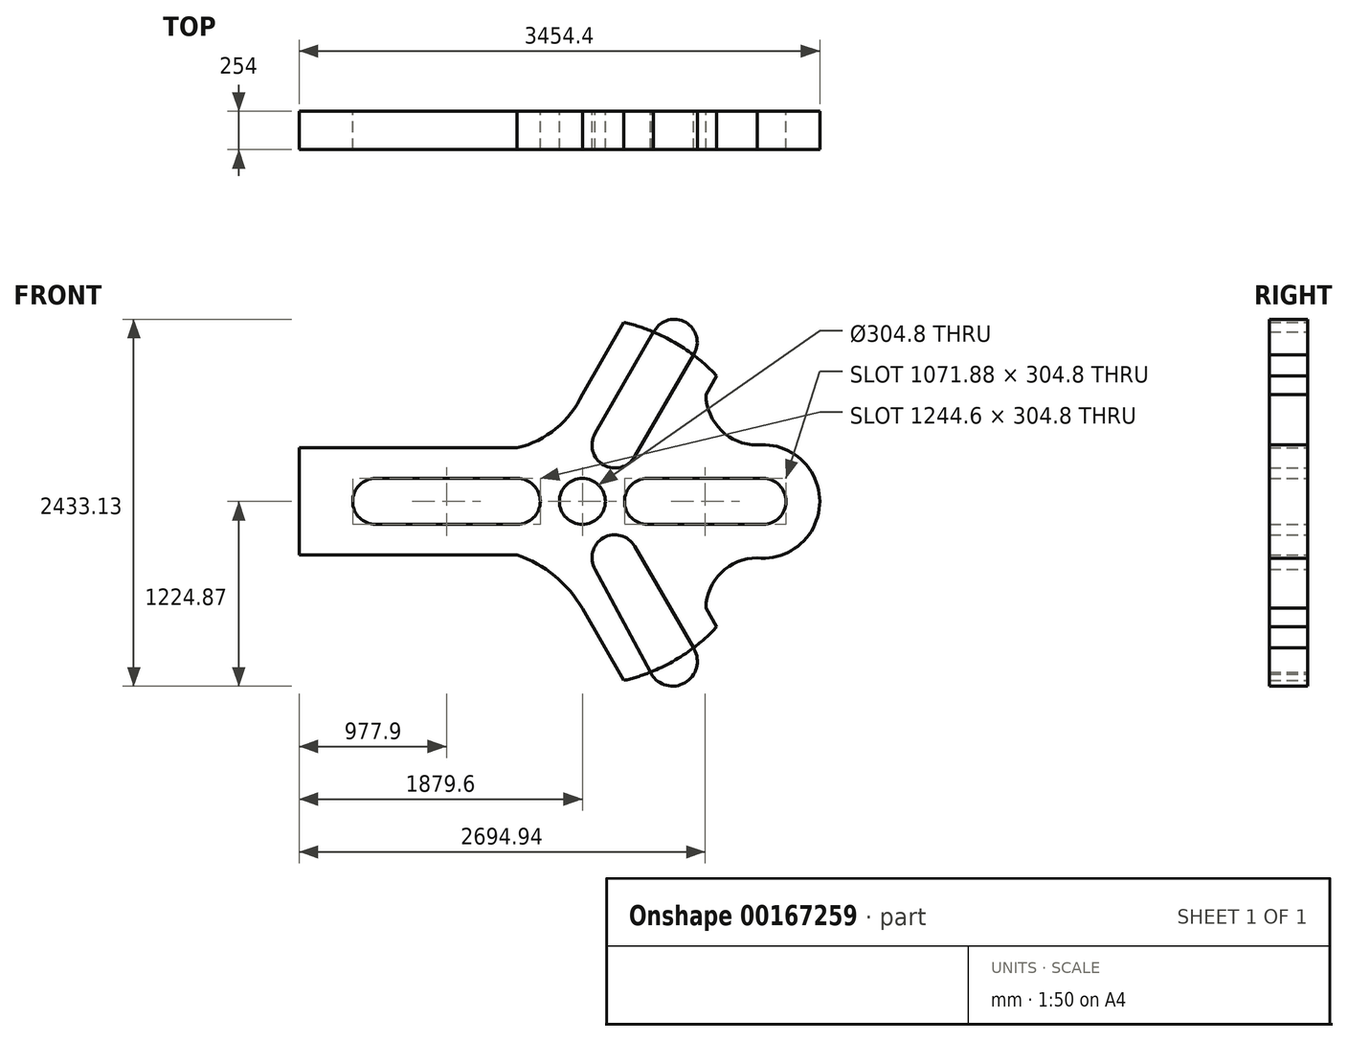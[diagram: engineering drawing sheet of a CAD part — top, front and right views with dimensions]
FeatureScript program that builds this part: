
annotation { "Feature Type Name" : "Feature", "Feature Type Description" : "" }
export const myFeature = defineFeature(function(context is Context, id is Id, definition is map)
    precondition{}
    {
        {
            var Q0;
            Q0=qCreatedBy(makeId("Front.planeOp"),FACE);
            var sketch = newSketch(context, id + "F0", { "sketchPlane" : qUnion([Q0])});
            skCircle(sketch, "E0", {"center": v(0, 0) * mm, "radius": 1219.2 * mm});
            skLineSegment(sketch, "E1", {"start": v(-1219.2, 0) * mm, "end": v(0, 0) * mm});
            skLineSegment(sketch, "E2", {"start": v(-1219.2, 0) * mm, "end": v(-1371.6, 0) * mm});
            skLineSegment(sketch, "E3", {"start": v(-1879.6, 0) * mm, "end": v(-1371.6, 0) * mm});
            skLineSegment(sketch, "E4", {"start": v(-1879.6, 0) * mm, "end": v(-1879.6, 355.6) * mm});
            skLineSegment(sketch, "E5", {"start": v(-1879.6, 0) * mm, "end": v(-1879.6, -355.6) * mm});
            skCircle(sketch, "E6", {"center": v(0, 0) * mm, "radius": 152.4 * mm});
            skCircle(sketch, "E7", {"center": v(0, 0) * mm, "radius": 431.8 * mm});
            skLineSegment(sketch, "E8", {"start": v(0, 0) * mm, "end": v(1574.8, 0) * mm});
            skLineSegment(sketch, "E9", {"start": v(-1879.6, 355.6) * mm, "end": v(-431.8, 355.6) * mm});
            skLineSegment(sketch, "E10", {"start": v(-1879.6, -355.6) * mm, "end": v(-431.8, -355.6) * mm});
            skLineSegment(sketch, "E11", {"start": v(0, 0) * mm, "end": v(609.6, 1055.86) * mm});
            skLineSegment(sketch, "E12", {"start": v(0, 0) * mm, "end": v(0, 1219.2) * mm});
            skLineSegment(sketch, "E13", {"start": v(609.6, 1055.86) * mm, "end": v(301.64, 1233.66) * mm});
            skLineSegment(sketch, "E14", {"start": v(301.64, 1233.66) * mm, "end": v(0, 711.2) * mm});
            skArc(sketch, "E15", {"start": v(-431.8, 355.6) * mm, "mid": v(-174.63, 483.3) * mm, "end": v(0, 711.2) * mm});
            skLineSegment(sketch, "E16", {"start": v(609.6, 1055.86) * mm, "end": v(917.56, 878.06) * mm});
            skArc(sketch, "E17", {"start": v(917.56, 878.06) * mm, "mid": v(787.4, 1363.82) * mm, "end": v(301.64, 1233.66) * mm});
            skLineSegment(sketch, "E18", {"start": v(0, 0) * mm, "end": v(0, -1219.2) * mm});
            skLineSegment(sketch, "E19", {"start": v(0, 0) * mm, "end": v(609.6, -1055.86) * mm});
            skLineSegment(sketch, "E20", {"start": v(609.6, -1055.86) * mm, "end": v(301.64, -1233.66) * mm});
            skLineSegment(sketch, "E21", {"start": v(609.6, -1055.86) * mm, "end": v(917.56, -878.06) * mm});
            skArc(sketch, "E22", {"start": v(301.64, -1233.66) * mm, "mid": v(787.4, -1363.82) * mm, "end": v(917.56, -878.06) * mm});
            skLineSegment(sketch, "E23", {"start": v(301.64, -1233.66) * mm, "end": v(0, -711.2) * mm});
            skArc(sketch, "E24", {"start": v(0, -711.2) * mm, "mid": v(-183.7, -494.3) * mm, "end": v(-431.8, -355.6) * mm});
            skLineSegment(sketch, "E25", {"start": v(215.9, -373.95) * mm, "end": v(609.6, -1055.86) * mm});
            skLineSegment(sketch, "E26", {"start": v(215.9, -373.95) * mm, "end": v(1160.44, -373.95) * mm});
            skLineSegment(sketch, "E27", {"start": v(609.6, -1055.86) * mm, "end": v(495.95, -859) * mm});
            skLineSegment(sketch, "E28", {"start": v(917.56, -878.06) * mm, "end": v(819.13, -707.58) * mm});
            skArc(sketch, "E29", {"start": v(1160.44, -373.95) * mm, "mid": v(921.8, -471.21) * mm, "end": v(819.13, -707.58) * mm});
            skLineSegment(sketch, "E30", {"start": v(215.9, 373.95) * mm, "end": v(1160.44, 373.95) * mm});
            skLineSegment(sketch, "E31", {"start": v(917.56, 878.06) * mm, "end": v(819.13, 707.58) * mm});
            skArc(sketch, "E32", {"start": v(819.13, 707.58) * mm, "mid": v(921.8, 471.21) * mm, "end": v(1160.44, 373.95) * mm});
            skArc(sketch, "E33", {"start": v(1160.44, -373.95) * mm, "mid": v(1574.8, 0) * mm, "end": v(1160.44, 373.95) * mm});
            skLineSegment(sketch, "E34", {"start": v(-1371.6, 0) * mm, "end": v(-1371.6, 152.4) * mm});
            skLineSegment(sketch, "E35", {"start": v(-1371.6, 0) * mm, "end": v(-1371.6, -152.4) * mm});
            skArc(sketch, "E36", {"start": v(-1371.6, 152.4) * mm, "mid": v(-1524, 0) * mm, "end": v(-1371.6, -152.4) * mm});
            skLineSegment(sketch, "E37", {"start": v(-431.8, 0) * mm, "end": v(-279.4, 0) * mm});
            skLineSegment(sketch, "E38", {"start": v(-431.8, 0) * mm, "end": v(-431.8, 152.4) * mm});
            skLineSegment(sketch, "E39", {"start": v(-431.8, 0) * mm, "end": v(-431.8, -152.4) * mm});
            skLineSegment(sketch, "E40", {"start": v(-1371.6, 152.4) * mm, "end": v(-431.8, 152.4) * mm});
            skLineSegment(sketch, "E41", {"start": v(-1371.6, -152.4) * mm, "end": v(-431.8, -152.4) * mm});
            skArc(sketch, "E42", {"start": v(-431.8, -152.4) * mm, "mid": v(-279.4, 0) * mm, "end": v(-431.8, 152.4) * mm});
            skLineSegment(sketch, "E43", {"start": v(609.6, 1055.86) * mm, "end": v(477.62, 1132.06) * mm});
            skLineSegment(sketch, "E44", {"start": v(609.6, 1055.86) * mm, "end": v(741.58, 979.66) * mm});
            skArc(sketch, "E45", {"start": v(741.58, 979.66) * mm, "mid": v(685.8, 1187.84) * mm, "end": v(477.62, 1132.06) * mm});
            skLineSegment(sketch, "E46", {"start": v(215.9, 373.95) * mm, "end": v(83.92, 450.15) * mm});
            skLineSegment(sketch, "E47", {"start": v(215.9, 373.95) * mm, "end": v(347.88, 297.75) * mm});
            skArc(sketch, "E48", {"start": v(83.92, 450.15) * mm, "mid": v(139.7, 241.97) * mm, "end": v(347.88, 297.75) * mm});
            skLineSegment(sketch, "E49", {"start": v(83.92, 450.15) * mm, "end": v(477.62, 1132.06) * mm});
            skLineSegment(sketch, "E50", {"start": v(347.88, 297.75) * mm, "end": v(741.58, 979.66) * mm});
            skLineSegment(sketch, "E51", {"start": v(609.6, -1055.86) * mm, "end": v(741.58, -979.66) * mm});
            skLineSegment(sketch, "E52", {"start": v(609.6, -1055.86) * mm, "end": v(457.2, -1143.85) * mm});
            skArc(sketch, "E53", {"start": v(457.2, -1143.85) * mm, "mid": v(680.86, -1202.87) * mm, "end": v(741.58, -979.66) * mm});
            skLineSegment(sketch, "E54", {"start": v(215.9, -373.95) * mm, "end": v(347.88, -297.75) * mm});
            skLineSegment(sketch, "E55", {"start": v(215.9, -373.95) * mm, "end": v(83.92, -450.15) * mm});
            skArc(sketch, "E56", {"start": v(347.88, -297.75) * mm, "mid": v(139.7, -241.97) * mm, "end": v(83.92, -450.15) * mm});
            skLineSegment(sketch, "E57", {"start": v(347.88, -297.75) * mm, "end": v(741.58, -979.66) * mm});
            skLineSegment(sketch, "E58", {"start": v(83.92, -450.15) * mm, "end": v(457.2, -1143.85) * mm});
            skLineSegment(sketch, "E59", {"start": v(1198.88, 0) * mm, "end": v(1198.88, 152.4) * mm});
            skLineSegment(sketch, "E60", {"start": v(1198.88, 0) * mm, "end": v(1198.88, -152.4) * mm});
            skArc(sketch, "E61", {"start": v(1198.88, -152.4) * mm, "mid": v(1351.28, 0) * mm, "end": v(1198.88, 152.4) * mm});
            skLineSegment(sketch, "E62", {"start": v(431.8, 0) * mm, "end": v(431.8, 152.4) * mm});
            skLineSegment(sketch, "E63", {"start": v(431.8, 0) * mm, "end": v(431.8, -152.4) * mm});
            skArc(sketch, "E64", {"start": v(431.8, 152.4) * mm, "mid": v(279.4, 0) * mm, "end": v(431.8, -152.4) * mm});
            skLineSegment(sketch, "E65", {"start": v(431.8, 152.4) * mm, "end": v(1198.88, 152.4) * mm});
            skLineSegment(sketch, "E66", {"start": v(431.8, -152.4) * mm, "end": v(1198.88, -152.4) * mm});
            skSolve(sketch);
        }
        {
            var Q0;
            {var subQ0=sQuery(id+"F0.wireOp",EDGE,"E33");var subQ5=sQuery(id+"F0.wireOp",EDGE,"E8");var subQ6=makeQuery(id+"F0.imprint","INTERSECT",VERTEX,{"derivedFrom":[subQ5,subQ0]});Q0=makeQuery(id+"F0.imprint","IMPRINT",FACE,{"disambiguationData":[TD([[makeQuery(id+"F0.imprint","IMPRINT",EDGE,{"disambiguationData":[TD([[subQ6,1.0]])],"derivedFrom":subQ5}),1.0]])]});}
            var Q1;
            {var subQ5=sQuery(id+"F0.wireOp",EDGE,"E16");Q1=makeQuery(id+"F0.imprint","IMPRINT",FACE,{"disambiguationData":[TD([[makeQuery(id+"F0.imprint","IMPRINT",EDGE,{"derivedFrom":subQ5}),-1.0]])]});}
            var Q2;
            {var subQ5=sQuery(id+"F0.wireOp",EDGE,"E13");Q2=makeQuery(id+"F0.imprint","IMPRINT",FACE,{"disambiguationData":[TD([[makeQuery(id+"F0.imprint","IMPRINT",EDGE,{"derivedFrom":subQ5}),1.0]])]});}
            var Q3;
            {var subQ5=sQuery(id+"F0.wireOp",EDGE,"E20");Q3=makeQuery(id+"F0.imprint","IMPRINT",FACE,{"disambiguationData":[TD([[makeQuery(id+"F0.imprint","IMPRINT",EDGE,{"derivedFrom":subQ5}),-1.0]])]});}
            var Q4;
            {var subQ5=sQuery(id+"F0.wireOp",EDGE,"E21");Q4=makeQuery(id+"F0.imprint","IMPRINT",FACE,{"disambiguationData":[TD([[makeQuery(id+"F0.imprint","IMPRINT",EDGE,{"derivedFrom":subQ5}),1.0]])]});}
            var Q5;
            {var subQ0=sQuery(id+"F0.wireOp",EDGE,"E33");var subQ5=sQuery(id+"F0.wireOp",EDGE,"E8");var subQ7=makeQuery(id+"F0.imprint","INTERSECT",VERTEX,{"derivedFrom":[subQ5,subQ0]});Q5=makeQuery(id+"F0.imprint","IMPRINT",FACE,{"disambiguationData":[TD([[makeQuery(id+"F0.imprint","IMPRINT",EDGE,{"disambiguationData":[TD([[subQ7,1.0]])],"derivedFrom":subQ5}),-1.0]])]});}
            var Q6;
            Q6=makeQuery(id+"F0.imprint","IMPRINT",FACE,{"disambiguationData":[TD([[makeQuery(id+"F0.imprint","IMPRINT",EDGE,{"derivedFrom":sQuery(id+"F0.wireOp",EDGE,"E13")}),-1.0]])]});
            var Q7;
            Q7=makeQuery(id+"F0.imprint","IMPRINT",FACE,{"disambiguationData":[TD([[makeQuery(id+"F0.imprint","IMPRINT",EDGE,{"derivedFrom":sQuery(id+"F0.wireOp",EDGE,"E20")}),1.0]])]});
            var Q8;
            {var subQ0=sQuery(id+"F0.wireOp",EDGE,"E32");Q8=makeQuery(id+"F0.imprint","IMPRINT",FACE,{"disambiguationData":[TD([[makeQuery(id+"F0.imprint","IMPRINT",EDGE,{"derivedFrom":subQ0}),-1.0]])]});}
            var Q9;
            {var subQ1=sQuery(id+"F0.wireOp",EDGE,"E4");Q9=makeQuery(id+"F0.imprint","IMPRINT",FACE,{"disambiguationData":[TD([[makeQuery(id+"F0.imprint","IMPRINT",EDGE,{"derivedFrom":subQ1}),-1.0]])]});}
            var Q10;
            {var subQ0=sQuery(id+"F0.wireOp",EDGE,"E5");Q10=makeQuery(id+"F0.imprint","IMPRINT",FACE,{"disambiguationData":[TD([[makeQuery(id+"F0.imprint","IMPRINT",EDGE,{"derivedFrom":subQ0}),1.0]])]});}
            var Q11;
            {var subQ0=sQuery(id+"F0.wireOp",EDGE,"E14");var subQ3=sQuery(id+"F0.wireOp",EDGE,"E0");var subQ4=makeQuery(id+"F0.imprint","INTERSECT",VERTEX,{"derivedFrom":[subQ3,subQ0]});Q11=makeQuery(id+"F0.imprint","IMPRINT",FACE,{"disambiguationData":[TD([[makeQuery(id+"F0.imprint","IMPRINT",EDGE,{"disambiguationData":[TD([[subQ4,1.0]])],"derivedFrom":subQ3}),1.0]])]});}
            var Q12;
            {var subQ0=sQuery(id+"F0.wireOp",EDGE,"E15");Q12=makeQuery(id+"F0.imprint","IMPRINT",FACE,{"disambiguationData":[TD([[makeQuery(id+"F0.imprint","IMPRINT",EDGE,{"derivedFrom":subQ0}),-1.0]])]});}
            var Q13;
            {var subQ0=sQuery(id+"F0.wireOp",EDGE,"E24");Q13=makeQuery(id+"F0.imprint","IMPRINT",FACE,{"disambiguationData":[TD([[makeQuery(id+"F0.imprint","IMPRINT",EDGE,{"derivedFrom":subQ0}),-1.0]])]});}
            var Q14;
            {var subQ0=sQuery(id+"F0.wireOp",EDGE,"E23");var subQ3=sQuery(id+"F0.wireOp",EDGE,"E0");var subQ4=makeQuery(id+"F0.imprint","INTERSECT",VERTEX,{"derivedFrom":[subQ3,subQ0]});Q14=makeQuery(id+"F0.imprint","IMPRINT",FACE,{"disambiguationData":[TD([[makeQuery(id+"F0.imprint","IMPRINT",EDGE,{"disambiguationData":[TD([[subQ4,-1.0]])],"derivedFrom":subQ3}),1.0]])]});}
            var Q15;
            {var subQ13=sQuery(id+"F0.wireOp",EDGE,"E65");Q15=makeQuery(id+"F0.imprint","IMPRINT",FACE,{"disambiguationData":[TD([[makeQuery(id+"F0.imprint","IMPRINT",EDGE,{"derivedFrom":subQ13}),1.0]])]});}
            var Q16;
            {var subQ5=sQuery(id+"F0.wireOp",EDGE,"E66");Q16=makeQuery(id+"F0.imprint","IMPRINT",FACE,{"disambiguationData":[TD([[makeQuery(id+"F0.imprint","IMPRINT",EDGE,{"derivedFrom":subQ5}),-1.0]])]});}
            var Q17;
            {var subQ1=sQuery(id+"F0.wireOp",EDGE,"E6");var subQ6=sQuery(id+"F0.wireOp",EDGE,"E1");var subQ9=makeQuery(id+"F0.imprint","INTERSECT",VERTEX,{"derivedFrom":[subQ6,subQ1]});Q17=makeQuery(id+"F0.imprint","IMPRINT",FACE,{"disambiguationData":[TD([[makeQuery(id+"F0.imprint","IMPRINT",EDGE,{"disambiguationData":[TD([[subQ9,-1.0]])],"derivedFrom":subQ1}),-1.0]])]});}
            var Q18;
            {var subQ1=sQuery(id+"F0.wireOp",EDGE,"E6");var subQ7=sQuery(id+"F0.wireOp",EDGE,"E1");var subQ8=makeQuery(id+"F0.imprint","INTERSECT",VERTEX,{"derivedFrom":[subQ7,subQ1]});Q18=makeQuery(id+"F0.imprint","IMPRINT",FACE,{"disambiguationData":[TD([[makeQuery(id+"F0.imprint","IMPRINT",EDGE,{"disambiguationData":[TD([[subQ8,1.0]])],"derivedFrom":subQ1}),-1.0]])]});}
            var Q19;
            {var subQ0=sQuery(id+"F0.wireOp",EDGE,"E11");var subQ1=sQuery(id+"F0.wireOp",EDGE,"E6");var subQ2=makeQuery(id+"F0.imprint","INTERSECT",VERTEX,{"derivedFrom":[subQ1,subQ0]});Q19=makeQuery(id+"F0.imprint","IMPRINT",FACE,{"disambiguationData":[TD([[makeQuery(id+"F0.imprint","IMPRINT",EDGE,{"disambiguationData":[TD([[subQ2,1.0]])],"derivedFrom":subQ1}),-1.0]])]});}
            var Q20;
            {var subQ1=sQuery(id+"F0.wireOp",EDGE,"E6");var subQ7=sQuery(id+"F0.wireOp",EDGE,"E11");var subQ8=makeQuery(id+"F0.imprint","INTERSECT",VERTEX,{"derivedFrom":[subQ1,subQ7]});Q20=makeQuery(id+"F0.imprint","IMPRINT",FACE,{"disambiguationData":[TD([[makeQuery(id+"F0.imprint","IMPRINT",EDGE,{"disambiguationData":[TD([[subQ8,-1.0]])],"derivedFrom":subQ1}),-1.0]])]});}
            var Q21;
            {var subQ6=sQuery(id+"F0.wireOp",EDGE,"E6");var subQ9=sQuery(id+"F0.wireOp",EDGE,"E8");var subQ10=makeQuery(id+"F0.imprint","INTERSECT",VERTEX,{"derivedFrom":[subQ6,subQ9]});Q21=makeQuery(id+"F0.imprint","IMPRINT",FACE,{"disambiguationData":[TD([[makeQuery(id+"F0.imprint","IMPRINT",EDGE,{"disambiguationData":[TD([[subQ10,1.0]])],"derivedFrom":subQ6}),-1.0]])]});}
            var Q22;
            {var subQ0=sQuery(id+"F0.wireOp",EDGE,"E18");var subQ1=sQuery(id+"F0.wireOp",EDGE,"E6");var subQ2=makeQuery(id+"F0.imprint","INTERSECT",VERTEX,{"derivedFrom":[subQ1,subQ0]});Q22=makeQuery(id+"F0.imprint","IMPRINT",FACE,{"disambiguationData":[TD([[makeQuery(id+"F0.imprint","IMPRINT",EDGE,{"disambiguationData":[TD([[subQ2,-1.0]])],"derivedFrom":subQ1}),-1.0]])]});}
            var Q23;
            {var subQ0=sQuery(id+"F0.wireOp",EDGE,"E29");Q23=makeQuery(id+"F0.imprint","IMPRINT",FACE,{"disambiguationData":[TD([[makeQuery(id+"F0.imprint","IMPRINT",EDGE,{"derivedFrom":subQ0}),-1.0]])]});}
            extrude(context, id + "F1", {"entities" : qUnion([Q0, Q1, Q2, Q3, Q4, Q5, Q6, Q7, Q8, Q9, Q10, Q11, Q12, Q13, Q14, Q15, Q16, Q17, Q18, Q19, Q20, Q21, Q22, Q23]), "depth" : 254 * mm});
        }
    });
